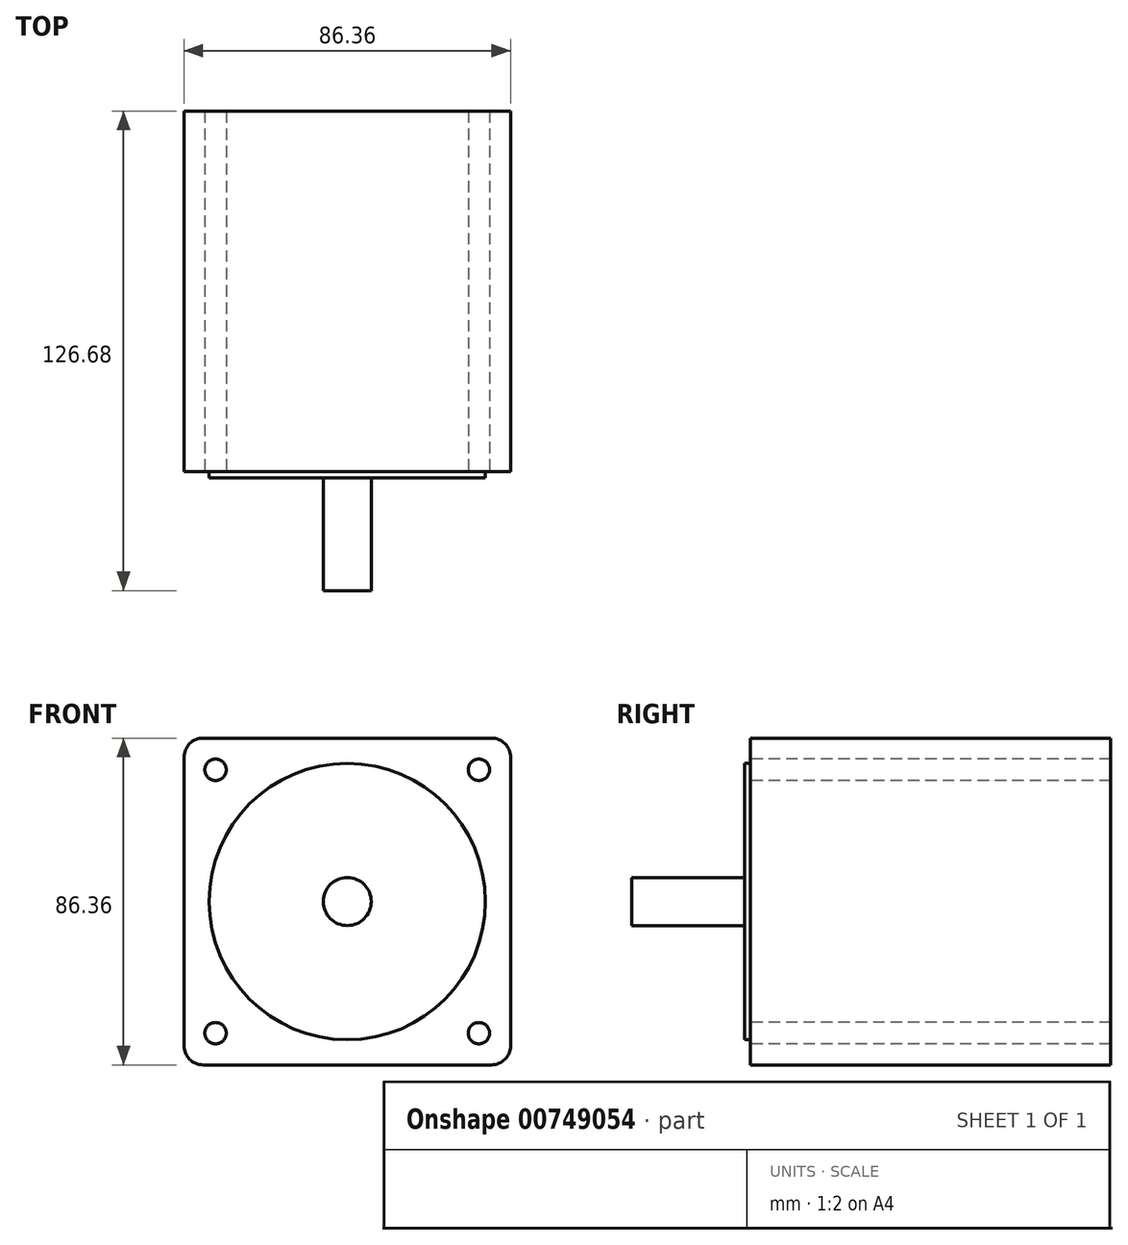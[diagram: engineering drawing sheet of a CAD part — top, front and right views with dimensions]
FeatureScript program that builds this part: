
annotation { "Feature Type Name" : "Feature", "Feature Type Description" : "" }
export const myFeature = defineFeature(function(context is Context, id is Id, definition is map)
    precondition{}
    {
        {
            var Q0;
            Q0=qCreatedBy(makeId("Front.planeOp"),FACE);
            var sketch = newSketch(context, id + "F0", { "sketchPlane" : qUnion([Q0])});
            skLineSegment(sketch, "E0.bottom", {"start": v(5.08, 0) * mm, "end": v(81.28, 0) * mm});
            skLineSegment(sketch, "E0.top", {"start": v(5.08, 86.36) * mm, "end": v(81.28, 86.36) * mm});
            skLineSegment(sketch, "E0.left", {"start": v(0, 5.08) * mm, "end": v(0, 81.28) * mm});
            skLineSegment(sketch, "E0.right", {"start": v(86.36, 5.08) * mm, "end": v(86.36, 81.28) * mm});
            skCircle(sketch, "E1", {"center": v(43.18, 43.18) * mm, "radius": 49.23 * mm, "construction": true});
            skPoint(sketch, "E1.centerSnap0", {"position": v(43.18, 0) * mm});
            skPoint(sketch, "E1.centerSnap1", {"position": v(0, 43.18) * mm});
            skLineSegment(sketch, "E2", {"start": v(0, 86.36) * mm, "end": v(86.36, 0) * mm, "construction": true});
            skLineSegment(sketch, "E3", {"start": v(86.36, 86.36) * mm, "end": v(0, 0) * mm, "construction": true});
            skCircle(sketch, "E4", {"center": v(8.37, 77.99) * mm, "radius": 2.83 * mm});
            skCircle(sketch, "E5", {"center": v(77.99, 77.99) * mm, "radius": 2.83 * mm});
            skCircle(sketch, "E6", {"center": v(77.99, 8.37) * mm, "radius": 2.83 * mm});
            skCircle(sketch, "E7", {"center": v(8.37, 8.37) * mm, "radius": 2.83 * mm});
            skPoint(sketch, "E8.visualSharp", {"position": v(0, 86.36) * mm});
            skArc(sketch, "E8.filletArc", {"start": v(5.08, 86.36) * mm, "mid": v(1.49, 84.87) * mm, "end": v(0, 81.28) * mm});
            skPoint(sketch, "E9.visualSharp", {"position": v(86.36, 86.36) * mm});
            skArc(sketch, "E9.filletArc", {"start": v(86.36, 81.28) * mm, "mid": v(84.87, 84.87) * mm, "end": v(81.28, 86.36) * mm});
            skPoint(sketch, "E10.visualSharp", {"position": v(86.36, 0) * mm});
            skArc(sketch, "E10.filletArc", {"start": v(81.28, 0) * mm, "mid": v(84.87, 1.49) * mm, "end": v(86.36, 5.08) * mm});
            skPoint(sketch, "E11.visualSharp", {"position": v(0, 0) * mm});
            skArc(sketch, "E11.filletArc", {"start": v(0, 5.08) * mm, "mid": v(1.49, 1.49) * mm, "end": v(5.08, 0) * mm});
            skSolve(sketch);
        }
        {
            var Q0;
            Q0 = qSketchRegion(id + "F0", true);
            extrude(context, id + "F1", {"entities" : qUnion([Q0]), "oppositeDirection" : true, "depth" : 95.25 * mm, "offsetDistance" : 25.4 * mm});
        }
        {
            var Q0;
            Q0=makeQuery(id+"F1.opExtrude","CAP_FACE",FACE,{"disambiguationData":[OSD([sQuery(id+"F0.wireOp",EDGE,"E0.bottom"),sQuery(id+"F0.wireOp",EDGE,"E0.top"),sQuery(id+"F0.wireOp",EDGE,"E0.left"),sQuery(id+"F0.wireOp",EDGE,"E0.right"),sQuery(id+"F0.wireOp",EDGE,"E4"),sQuery(id+"F0.wireOp",EDGE,"E5"),sQuery(id+"F0.wireOp",EDGE,"E6"),sQuery(id+"F0.wireOp",EDGE,"E7"),sQuery(id+"F0.wireOp",EDGE,"E8.filletArc"),sQuery(id+"F0.wireOp",EDGE,"E9.filletArc"),sQuery(id+"F0.wireOp",EDGE,"E10.filletArc"),sQuery(id+"F0.wireOp",EDGE,"E11.filletArc")])],"isStart":true});
            var sketch = newSketch(context, id + "F2", { "sketchPlane" : qUnion([Q0])});
            skCircle(sketch, "E12", {"center": v(43.18, 43.18) * mm, "radius": 36.51 * mm});
            skPoint(sketch, "E12.centerSnap0", {"position": v(43.18, 0) * mm});
            skPoint(sketch, "E12.centerSnap1", {"position": v(0, 43.18) * mm});
            skSolve(sketch);
        }
        {
            var Q0;
            Q0 = qSketchRegion(id + "F2", true);
            extrude(context, id + "F3", {"entities" : qUnion([Q0]), "operationType" : NewBodyOperationType.ADD, "depth" : 1.59 * mm, "offsetDistance" : 25.4 * mm});
        }
        {
            var Q0;
            Q0=makeQuery(id+"F3.opExtrude","CAP_FACE",FACE,{"disambiguationData":[OSD([sQuery(id+"F2.wireOp",EDGE,"E12")])],"isStart":false});
            var sketch = newSketch(context, id + "F4", { "sketchPlane" : qUnion([Q0])});
            skCircle(sketch, "E13", {"center": v(43.18, 43.18) * mm, "radius": 6.35 * mm});
            skSolve(sketch);
        }
        {
            var Q0;
            Q0 = qSketchRegion(id + "F4", true);
            extrude(context, id + "F5", {"entities" : qUnion([Q0]), "operationType" : NewBodyOperationType.ADD, "depth" : 29.84 * mm, "offsetDistance" : 25.4 * mm});
        }
    });
